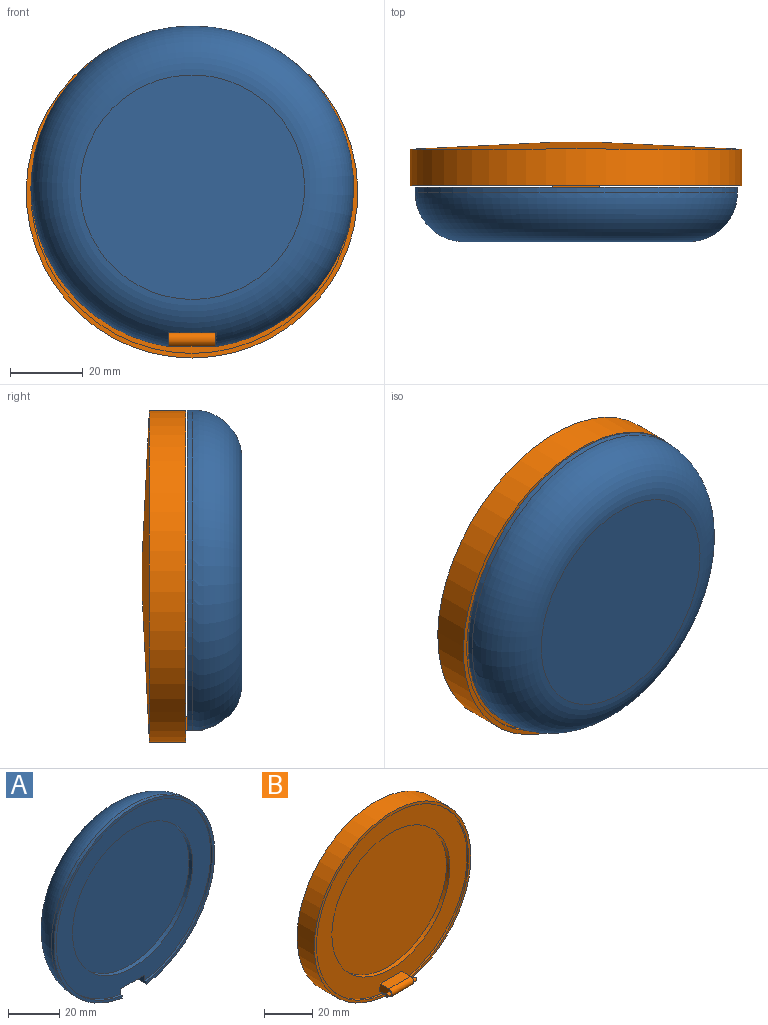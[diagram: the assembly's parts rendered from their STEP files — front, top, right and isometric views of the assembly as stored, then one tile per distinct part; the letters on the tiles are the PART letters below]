
ASSEMBLY  parts=2 mates=1
PART A: 15 faces, bbox 96.2x23.1x96.2 mm
  f0: plane 13.23x10.44mm, normal (0,0,-1), area 135.8mm2, adj f4,f6,f9,f12
  f1: cylinder r=44.45mm len=88.9mm, axis (0,1,0), area 401.5mm2, adj f2,f4,f9,f12
  f2: plane 88.9x88.41mm, normal (0,-1,0), area 332.1mm2, adj f1,f4,f5,f12
  f3: plane 61.92x61.92mm, normal (0,1,0), area 3011.2mm2, adj f9
  f4: plane 10.92x3.87mm, normal (1,0,0), area 26.3mm2, adj f0,f1,f2,f5,f6,f9,f11
  f5: cylinder r=43.18mm len=86.37mm, axis (0,-1,0), area 258.1mm2, adj f2,f4,f6,f12
  f6: plane 86.37x85.86mm, normal (0,-1,0), area 2358.5mm2, adj f0,f4,f5,f7,f12
  f7: cylinder r=33.19mm len=66.38mm, axis (0,-1,0), area 417.1mm2, adj f6,f8
  f8: plane 66.38x66.38mm, normal (0,-1,0), area 3461.1mm2, adj f7
  f9: torus R=30.96mm, axis (0,-1,0), area 5120.9mm2, adj f0,f1,f3,f4,f12
  f10: cone r=0mm half-angle=59deg, axis (1,0,0), area 2.3mm2, adj f11
  f11: cylinder r=0.79mm len=3.5mm, axis (1,0,0), area 17.5mm2, adj f4,f10
  f12: plane 10.91x3.87mm, normal (-1,0,0), area 26.3mm2, adj f0,f1,f2,f5,f6,f9,f14
  f13: cone r=0mm half-angle=59deg, axis (-1,0,0), area 2.3mm2, adj f14
  f14: cylinder r=0.79mm len=3.5mm, axis (-1,0,0), area 17.5mm2, adj f12,f13
PART B: 17 faces, bbox 91.4x18x91.4 mm
  f0: plane 7.03x3.84mm, normal (1,0,0), area 23.3mm2, adj f3,f5,f7,f14,f16
  f1: cylinder r=45.72mm len=91.44mm, axis (0,1,0), area 2872.7mm2, adj f2,f11
  f2: plane 91.44x91.44mm, normal (0,-1,0), area 359.8mm2, adj f1,f6
  f3: plane 12.7x5.13mm, normal (0,0,-1), area 65.2mm2, adj f0,f4,f7,f16
  f4: plane 7.03x3.84mm, normal (-1,0,0), area 23.3mm2, adj f3,f5,f7,f12,f16
  f5: plane 12.7x5.13mm, normal (0,0,1), area 65.2mm2, adj f0,f4,f7,f16
  f6: cylinder r=44.45mm len=88.9mm, axis (0,-1,0), area 279.3mm2, adj f2,f7
  f7: plane 88.9x88.9mm, normal (0,-1,0), area 2430mm2, adj f0,f3,f4,f5,f6,f8
  f8: cylinder r=34.45mm len=68.9mm, axis (0,-1,0), area 432.9mm2, adj f7,f9
  f9: plane 68.9x68.9mm, normal (0,-1,0), area 3728.5mm2, adj f8
  f10: plane 9.16x9.16mm, normal (0,1,0), area 65.9mm2, adj f11
  f11: cone r=4.58mm half-angle=87.2deg, axis (0,-1,0), area 6508.7mm2, adj f1,f10
  f12: cylinder r=0.82mm len=2mm, axis (1,0,0), area 10.4mm2, adj f4,f13
  f13: plane 1.65x1.65mm, normal (-1,0,0), area 2.1mm2, adj f12
  f14: cylinder r=0.82mm len=2mm, axis (-1,0,0), area 10.4mm2, adj f0,f15
  f15: plane 1.65x1.65mm, normal (1,0,0), area 2.1mm2, adj f14
  f16: cylinder r=1.92mm len=12.7mm, axis (-1,0,0), area 76mm2, adj f0,f3,f4,f5
PLACE A rot(axis=(0,0,-1),180deg) t=(-39.53,25.54,-4.91)mm
PLACE B t=(-39.63,51.06,-6.3)mm
MATE pin_slot A.f13 <-> B.f12  axis (1,0,0) through (-47.98,36.1,-46.92)mm
